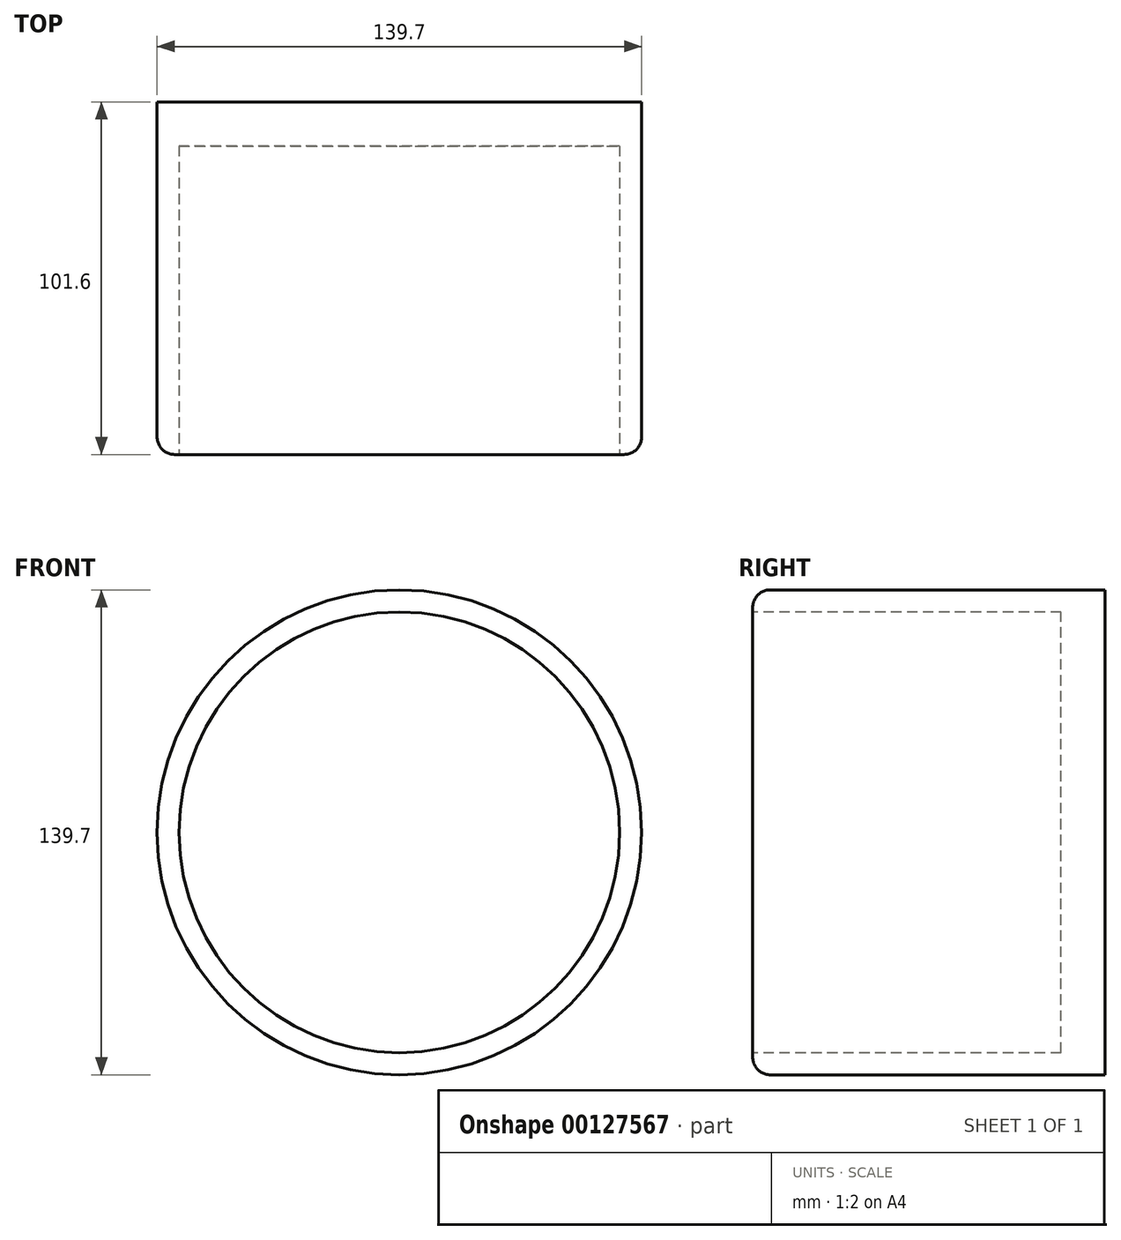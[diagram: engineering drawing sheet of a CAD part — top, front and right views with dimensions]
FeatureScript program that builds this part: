
annotation { "Feature Type Name" : "Feature", "Feature Type Description" : "" }
export const myFeature = defineFeature(function(context is Context, id is Id, definition is map)
    precondition{}
    {
        {
            var Q0;
            Q0=qCreatedBy(makeId("Front.planeOp"),FACE);
            var sketch = newSketch(context, id + "F0", { "sketchPlane" : qUnion([Q0])});
            skCircle(sketch, "E0", {"center": v(0, 0) * mm, "radius": 69.85 * mm});
            skSolve(sketch);
        }
        {
            var Q0;
            Q0 = qSketchRegion(id + "F0", true);
            extrude(context, id + "F1", {"entities" : qUnion([Q0]), "depth" : 101.6 * mm});
        }
        {
            var Q0;
            Q0=makeQuery(id+"F1.opExtrude","CAP_FACE",FACE,{"disambiguationData":[OSD([sQuery(id+"F0.wireOp",EDGE,"E0")])],"isStart":false});
            var sketch = newSketch(context, id + "F2", { "sketchPlane" : qUnion([Q0])});
            skCircle(sketch, "E1.0", {"center": v(0, 0) * mm, "radius": 63.5 * mm});
            skSolve(sketch);
        }
        {
            var Q0;
            Q0=makeQuery(id+"F2.imprint","IMPRINT",FACE,{"disambiguationData":[TD([[makeQuery(id+"F2.imprint","IMPRINT",EDGE,{"derivedFrom":sQuery(id+"F2.wireOp",EDGE,"E1.0")}),1.0]])]});
            extrude(context, id + "F3", {"entities" : qUnion([Q0]), "operationType" : NewBodyOperationType.REMOVE, "oppositeDirection" : true, "depth" : 88.9 * mm});
        }
        {
            var Q0;
            Q0=makeQuery(id+"F1.opExtrude","CAP_EDGE",EDGE,{"disambiguationData":[OSD([sQuery(id+"F0.wireOp",EDGE,"E0")])],"isStart":false});
            fillet(context, id + "F4", {"entities" : qUnion([Q0]), "radius" : 5.08 * mm, "tangentPropagation" : true, "allowEdgeOverflow" : false});
        }
    });
